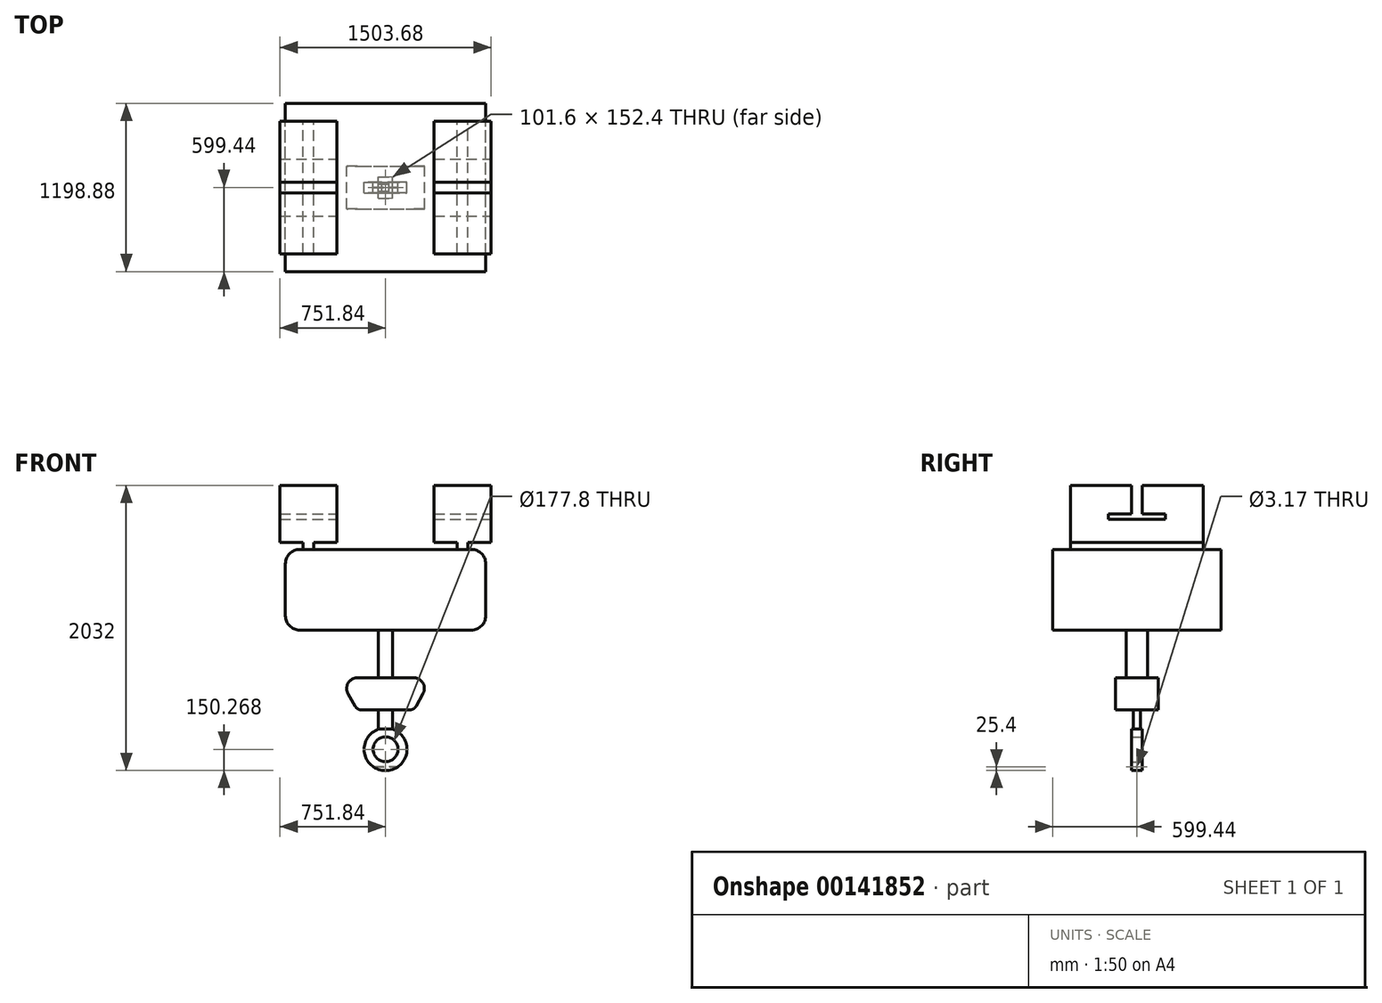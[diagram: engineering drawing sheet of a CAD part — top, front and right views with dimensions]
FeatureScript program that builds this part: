
annotation { "Feature Type Name" : "Feature", "Feature Type Description" : "" }
export const myFeature = defineFeature(function(context is Context, id is Id, definition is map)
    precondition{}
    {
        {
            var Q0;
            Q0=qCreatedBy(makeId("Front.planeOp"),FACE);
            var sketch = newSketch(context, id + "F0", { "sketchPlane" : qUnion([Q0])});
            skLineSegment(sketch, "E0", {"start": v(0, 0) * mm, "end": v(0, -1397) * mm, "construction": true});
            skLineSegment(sketch, "E1.bottom", {"start": v(345.44, 203.2) * mm, "end": v(751.84, 203.2) * mm});
            skLineSegment(sketch, "E1.top", {"start": v(345.44, -203.2) * mm, "end": v(510.54, -203.2) * mm});
            skLineSegment(sketch, "E1.left", {"start": v(345.44, 203.2) * mm, "end": v(345.44, -203.2) * mm});
            skLineSegment(sketch, "E1.right", {"start": v(751.84, 203.2) * mm, "end": v(751.84, -203.2) * mm});
            skLineSegment(sketch, "E2.bottom", {"start": v(0, -254) * mm, "end": v(510.54, -254) * mm});
            skLineSegment(sketch, "E2.top", {"start": v(50.8, -828.04) * mm, "end": v(612.14, -828.04) * mm});
            skLineSegment(sketch, "E2.right", {"start": v(713.74, -355.6) * mm, "end": v(713.74, -726.44) * mm});
            skLineSegment(sketch, "E3", {"start": v(0, 0) * mm, "end": v(345.44, 0) * mm, "construction": true});
            skLineSegment(sketch, "E4", {"start": v(50.8, -1397) * mm, "end": v(173.3, -1397) * mm});
            skLineSegment(sketch, "E5", {"start": v(217.72, -1370.87) * mm, "end": v(267.3, -1281.6) * mm});
            skLineSegment(sketch, "E6", {"start": v(200.7, -1168.4) * mm, "end": v(50.8, -1168.4) * mm});
            skLineSegment(sketch, "E7.left", {"start": v(510.54, -203.2) * mm, "end": v(510.54, -254) * mm});
            skLineSegment(sketch, "E7.right", {"start": v(586.74, -203.2) * mm, "end": v(586.74, -254) * mm});
            skLineSegment(sketch, "E8.trimOffspring", {"start": v(586.74, -203.2) * mm, "end": v(751.84, -203.2) * mm});
            skLineSegment(sketch, "E9.trimOffspring", {"start": v(586.74, -254) * mm, "end": v(612.14, -254) * mm});
            skPoint(sketch, "E10.visualSharp", {"position": v(330.2, -1168.4) * mm});
            skArc(sketch, "E10.filletArc", {"start": v(267.3, -1281.6) * mm, "mid": v(266.37, -1205.96) * mm, "end": v(200.7, -1168.4) * mm});
            skPoint(sketch, "E11.visualSharp", {"position": v(203.2, -1397) * mm});
            skArc(sketch, "E11.filletArc", {"start": v(173.3, -1397) * mm, "mid": v(199.07, -1389.98) * mm, "end": v(217.72, -1370.87) * mm});
            skPoint(sketch, "E12.visualSharp", {"position": v(713.74, -828.04) * mm});
            skArc(sketch, "E12.filletArc", {"start": v(612.14, -828.04) * mm, "mid": v(683.98, -798.28) * mm, "end": v(713.74, -726.44) * mm});
            skPoint(sketch, "E13.visualSharp", {"position": v(713.74, -254) * mm});
            skArc(sketch, "E13.filletArc", {"start": v(713.74, -355.6) * mm, "mid": v(683.98, -283.76) * mm, "end": v(612.14, -254) * mm});
            skArc(sketch, "E14", {"start": v(0, -1767.43) * mm, "mid": v(88.9, -1678.53) * mm, "end": v(0, -1589.63) * mm});
            skArc(sketch, "E15", {"start": v(25.4, -1828.8) * mm, "mid": v(151.83, -1691.65) * mm, "end": v(50.8, -1534.85) * mm});
            skLineSegment(sketch, "E16", {"start": v(0, -1397) * mm, "end": v(0, -1830.93) * mm, "construction": true});
            skLineSegment(sketch, "E17", {"start": v(50.8, -1397) * mm, "end": v(50.8, -1534.85) * mm});
            skArc(sketch, "E18.MirrorCS", {"start": v(-173.3, -1397) * mm, "mid": v(-199.07, -1389.98) * mm, "end": v(-217.72, -1370.87) * mm});
            skLineSegment(sketch, "E19.MirrorCS", {"start": v(-586.74, -203.2) * mm, "end": v(-586.74, -254) * mm});
            skLineSegment(sketch, "E20.MirrorCS", {"start": v(-586.74, -254) * mm, "end": v(-612.14, -254) * mm});
            skLineSegment(sketch, "E21.MirrorCS", {"start": v(-510.54, -203.2) * mm, "end": v(-510.54, -254) * mm});
            skLineSegment(sketch, "E22.MirrorCS", {"start": v(-217.72, -1370.87) * mm, "end": v(-267.3, -1281.6) * mm});
            skArc(sketch, "E23.MirrorCS", {"start": v(-713.74, -355.6) * mm, "mid": v(-683.98, -283.76) * mm, "end": v(-612.14, -254) * mm});
            skArc(sketch, "E24.MirrorCS", {"start": v(-612.14, -828.04) * mm, "mid": v(-683.98, -798.28) * mm, "end": v(-713.74, -726.44) * mm});
            skLineSegment(sketch, "E25.MirrorCS", {"start": v(-345.44, 203.2) * mm, "end": v(-345.44, -203.2) * mm});
            skLineSegment(sketch, "E26.MirrorCS", {"start": v(-200.7, -1168.4) * mm, "end": v(-50.8, -1168.4) * mm});
            skPoint(sketch, "E27.MirrorP", {"position": v(-713.74, -828.04) * mm});
            skArc(sketch, "E28.MirrorCS", {"start": v(0, -1767.43) * mm, "mid": v(-88.9, -1678.53) * mm, "end": v(0, -1589.63) * mm});
            skPoint(sketch, "E29.MirrorP", {"position": v(-713.74, -254) * mm});
            skLineSegment(sketch, "E30.MirrorCS", {"start": v(-345.44, 203.2) * mm, "end": v(-751.84, 203.2) * mm});
            skPoint(sketch, "E31.MirrorP", {"position": v(-203.2, -1397) * mm});
            skLineSegment(sketch, "E32.MirrorCS", {"start": v(-586.74, -203.2) * mm, "end": v(-751.84, -203.2) * mm});
            skLineSegment(sketch, "E33.MirrorCS", {"start": v(-50.8, -1397) * mm, "end": v(-173.3, -1397) * mm});
            skLineSegment(sketch, "E34.MirrorCS", {"start": v(0, 0) * mm, "end": v(-345.44, 0) * mm, "construction": true});
            skLineSegment(sketch, "E35.MirrorCS", {"start": v(-50.8, -1397) * mm, "end": v(-50.8, -1534.85) * mm});
            skLineSegment(sketch, "E36.MirrorCS", {"start": v(0, -254) * mm, "end": v(-510.54, -254) * mm});
            skLineSegment(sketch, "E37.MirrorCS", {"start": v(-345.44, -203.2) * mm, "end": v(-510.54, -203.2) * mm});
            skLineSegment(sketch, "E38.MirrorCS", {"start": v(-713.74, -355.6) * mm, "end": v(-713.74, -726.44) * mm});
            skLineSegment(sketch, "E39.MirrorCS", {"start": v(-50.8, -828.04) * mm, "end": v(-612.14, -828.04) * mm});
            skPoint(sketch, "E40.MirrorP", {"position": v(-330.2, -1168.4) * mm});
            skArc(sketch, "E41.MirrorCS", {"start": v(-25.4, -1828.8) * mm, "mid": v(-151.83, -1691.65) * mm, "end": v(-50.8, -1534.85) * mm});
            skLineSegment(sketch, "E42.MirrorCS", {"start": v(-751.84, 203.2) * mm, "end": v(-751.84, -203.2) * mm});
            skArc(sketch, "E43.MirrorCS", {"start": v(-267.3, -1281.6) * mm, "mid": v(-266.37, -1205.96) * mm, "end": v(-200.7, -1168.4) * mm});
            skLineSegment(sketch, "E44", {"start": v(50.8, -828.04) * mm, "end": v(50.8, -1168.4) * mm});
            skLineSegment(sketch, "E45", {"start": v(-50.8, -828.04) * mm, "end": v(-50.8, -1168.4) * mm});
            skPoint(sketch, "E46.orphan", {"position": v(0, -828.04) * mm});
            skPoint(sketch, "E47.orphan", {"position": v(0, -1168.4) * mm});
            skLineSegment(sketch, "E48", {"start": v(-25.4, -1828.8) * mm, "end": v(25.4, -1828.8) * mm});
            skSolve(sketch);
        }
        {
            var Q0;
            Q0 = qSketchRegion(id + "F0", true);
            extrude(context, id + "F1", {"entities" : qUnion([Q0]), "depth" : 1198.88 * mm, "symmetric" : true});
        }
        {
            var Q0;
            Q0=qCreatedBy(makeId("Right.planeOp"),FACE);
            var sketch = newSketch(context, id + "F2", { "sketchPlane" : qUnion([Q0])});
            skLineSegment(sketch, "E49", {"start": v(0, -38.1) * mm, "end": v(0, -1699.83) * mm, "construction": true});
            skLineSegment(sketch, "E50.bottom", {"start": v(599.44, 203.2) * mm, "end": v(472.44, 203.2) * mm});
            skLineSegment(sketch, "E50.top", {"start": v(599.44, -254) * mm, "end": v(472.44, -254) * mm});
            skLineSegment(sketch, "E50.left", {"start": v(599.44, 203.2) * mm, "end": v(599.44, -254) * mm});
            skLineSegment(sketch, "E50.right", {"start": v(472.44, 203.2) * mm, "end": v(472.44, -254) * mm});
            skLineSegment(sketch, "E51.bottom", {"start": v(599.44, -828.04) * mm, "end": v(152.4, -828.04) * mm});
            skLineSegment(sketch, "E51.top", {"start": v(599.44, -1828.8) * mm, "end": v(38.1, -1828.8) * mm});
            skLineSegment(sketch, "E51.left", {"start": v(599.44, -828.04) * mm, "end": v(599.44, -1828.8) * mm});
            skLineSegment(sketch, "E51.right", {"start": v(152.4, -1168.4) * mm, "end": v(152.4, -1397) * mm});
            skLineSegment(sketch, "E52.bottom", {"start": v(152.4, -828.04) * mm, "end": v(76.2, -828.04) * mm});
            skLineSegment(sketch, "E52.top", {"start": v(152.4, -1168.4) * mm, "end": v(76.2, -1168.4) * mm});
            skLineSegment(sketch, "E52.right", {"start": v(76.2, -828.04) * mm, "end": v(76.2, -1168.4) * mm});
            skLineSegment(sketch, "E53.bottom", {"start": v(152.4, -1397) * mm, "end": v(25.4, -1397) * mm});
            skLineSegment(sketch, "E53.top", {"start": v(38.1, -1534.85) * mm, "end": v(25.4, -1534.85) * mm});
            skLineSegment(sketch, "E53.right", {"start": v(25.4, -1397) * mm, "end": v(25.4, -1534.85) * mm});
            skLineSegment(sketch, "E54.bottom", {"start": v(38.1, 0) * mm, "end": v(203.2, 0) * mm});
            skLineSegment(sketch, "E54.top", {"start": v(0, -38.1) * mm, "end": v(203.2, -38.1) * mm});
            skLineSegment(sketch, "E54.right", {"start": v(203.2, 0) * mm, "end": v(203.2, -38.1) * mm});
            skLineSegment(sketch, "E55.top", {"start": v(0, 203.2) * mm, "end": v(38.1, 203.2) * mm});
            skLineSegment(sketch, "E55.right", {"start": v(38.1, 0) * mm, "end": v(38.1, 203.2) * mm});
            skLineSegment(sketch, "E56.trimOffspring", {"start": v(38.1, -1534.85) * mm, "end": v(38.1, -1828.8) * mm});
            skLineSegment(sketch, "E57.MirrorCS", {"start": v(-152.4, -828.04) * mm, "end": v(-76.2, -828.04) * mm});
            skLineSegment(sketch, "E58.MirrorCS", {"start": v(-152.4, -1168.4) * mm, "end": v(-76.2, -1168.4) * mm});
            skLineSegment(sketch, "E59.MirrorCS", {"start": v(-38.1, -1534.85) * mm, "end": v(-25.4, -1534.85) * mm});
            skLineSegment(sketch, "E60.MirrorCS", {"start": v(-152.4, -1397) * mm, "end": v(-25.4, -1397) * mm});
            skLineSegment(sketch, "E61.MirrorCS", {"start": v(-203.2, 0) * mm, "end": v(-203.2, -38.1) * mm});
            skLineSegment(sketch, "E62.MirrorCS", {"start": v(0, 203.2) * mm, "end": v(-38.1, 203.2) * mm});
            skLineSegment(sketch, "E63.MirrorCS", {"start": v(-472.44, 203.2) * mm, "end": v(-472.44, -254) * mm});
            skLineSegment(sketch, "E64.MirrorCS", {"start": v(-599.44, 203.2) * mm, "end": v(-599.44, -254) * mm});
            skLineSegment(sketch, "E65.MirrorCS", {"start": v(-599.44, -254) * mm, "end": v(-472.44, -254) * mm});
            skLineSegment(sketch, "E66.MirrorCS", {"start": v(-599.44, 203.2) * mm, "end": v(-472.44, 203.2) * mm});
            skLineSegment(sketch, "E67.MirrorCS", {"start": v(-152.4, -1168.4) * mm, "end": v(-152.4, -1397) * mm});
            skLineSegment(sketch, "E68.MirrorCS", {"start": v(-599.44, -828.04) * mm, "end": v(-152.4, -828.04) * mm});
            skLineSegment(sketch, "E69.MirrorCS", {"start": v(-76.2, -828.04) * mm, "end": v(-76.2, -1168.4) * mm});
            skLineSegment(sketch, "E70.MirrorCS", {"start": v(-38.1, 0) * mm, "end": v(-203.2, 0) * mm});
            skLineSegment(sketch, "E71.MirrorCS", {"start": v(-25.4, -1397) * mm, "end": v(-25.4, -1534.85) * mm});
            skLineSegment(sketch, "E72.MirrorCS", {"start": v(-38.1, -1534.85) * mm, "end": v(-38.1, -1828.8) * mm});
            skLineSegment(sketch, "E73.MirrorCS", {"start": v(-599.44, -1828.8) * mm, "end": v(-38.1, -1828.8) * mm});
            skLineSegment(sketch, "E74.MirrorCS", {"start": v(0, -38.1) * mm, "end": v(-203.2, -38.1) * mm});
            skLineSegment(sketch, "E75.MirrorCS", {"start": v(-38.1, 0) * mm, "end": v(-38.1, 203.2) * mm});
            skLineSegment(sketch, "E76.MirrorCS", {"start": v(-599.44, -828.04) * mm, "end": v(-599.44, -1828.8) * mm});
            skPoint(sketch, "E54.left.start.orphan", {"position": v(0, 0) * mm});
            skCircle(sketch, "E77", {"center": v(0, -1803.4) * mm, "radius": 1.59 * mm});
            skLineSegment(sketch, "E78", {"start": v(599.44, -1767.43) * mm, "end": v(-599.44, -1767.43) * mm, "construction": true});
            skLineSegment(sketch, "E79", {"start": v(-599.44, -1589.63) * mm, "end": v(599.44, -1589.63) * mm, "construction": true});
            skSolve(sketch);
        }
        {
            var Q0;
            Q0 = qSketchRegion(id + "F2", true);
            extrude(context, id + "F3", {"entities" : qUnion([Q0]), "operationType" : NewBodyOperationType.REMOVE, "endBound" : BoundingType.THROUGH_ALL, "oppositeDirection" : true, "depth" : 25.4 * mm, "hasSecondDirection" : true, "secondDirectionBound" : BoundingType.THROUGH_ALL, "secondDirectionOppositeDirection" : false, "secondDirectionDepth" : 25.4 * mm});
        }
    });
